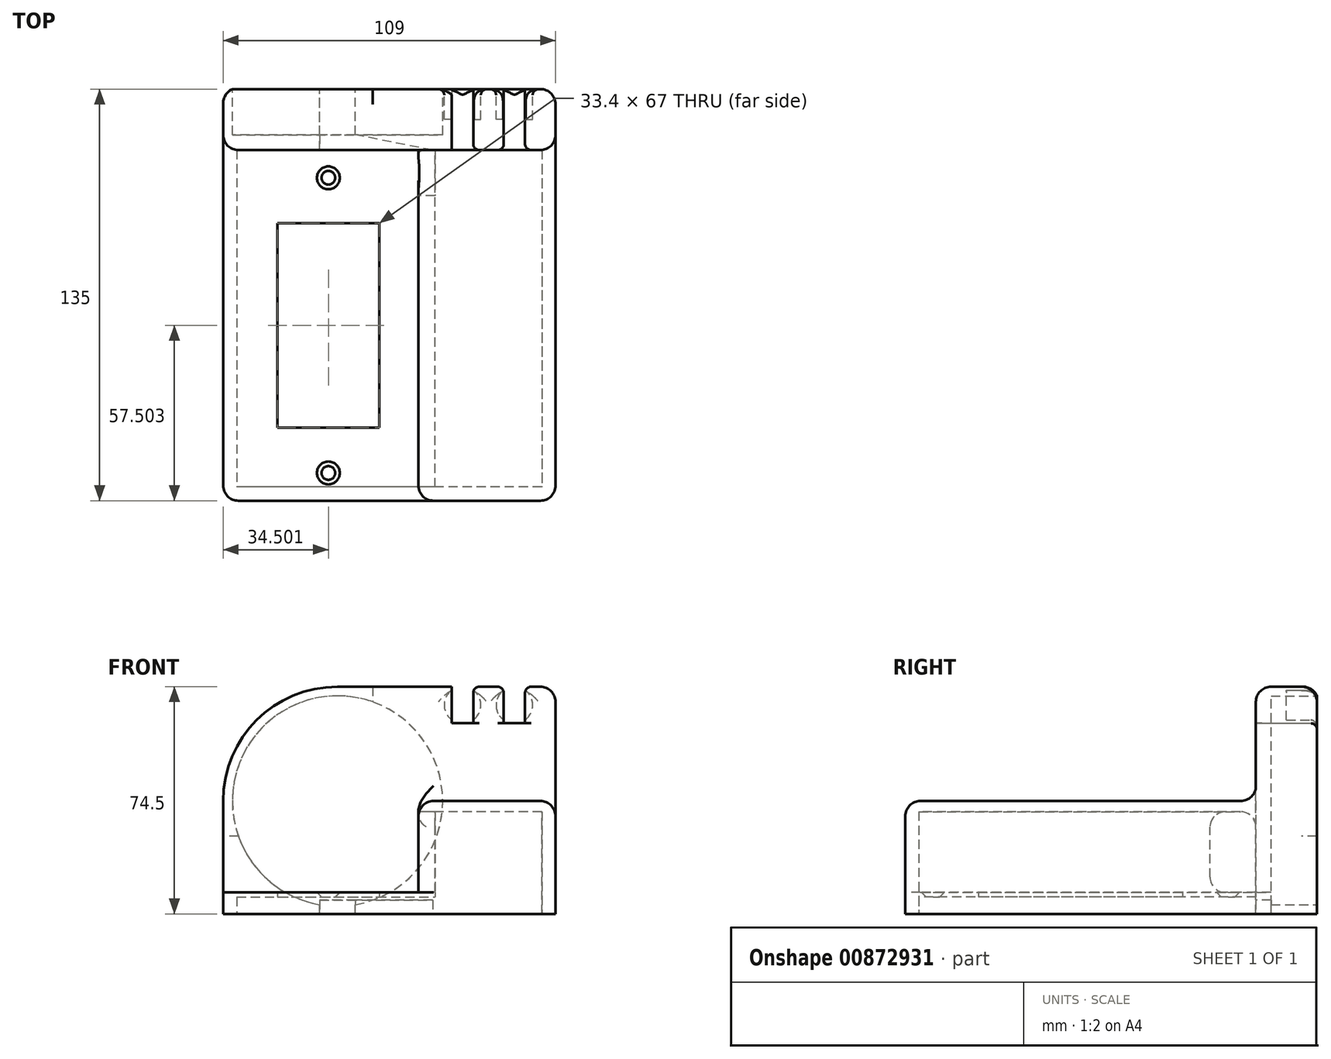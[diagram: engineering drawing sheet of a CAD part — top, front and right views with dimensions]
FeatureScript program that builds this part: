
annotation { "Feature Type Name" : "Feature", "Feature Type Description" : "" }
export const myFeature = defineFeature(function(context is Context, id is Id, definition is map)
    precondition{}
    {
        {
            var Q0;
            Q0=qCreatedBy(makeId("Top.planeOp"),FACE);
            var sketch = newSketch(context, id + "F0", { "sketchPlane" : qUnion([Q0])});
            skLineSegment(sketch, "E0.top", {"start": v(-268.4, -118.47) * mm, "end": v(-199.4, -118.47) * mm});
            skLineSegment(sketch, "E0.left", {"start": v(-268.4, -3.47) * mm, "end": v(-268.4, -118.47) * mm});
            skLineSegment(sketch, "E1.bottom", {"start": v(-217.2, -94.47) * mm, "end": v(-250.6, -94.47) * mm});
            skLineSegment(sketch, "E1.top", {"start": v(-217.2, -27.47) * mm, "end": v(-250.6, -27.47) * mm});
            skLineSegment(sketch, "E1.left", {"start": v(-217.2, -94.47) * mm, "end": v(-217.2, -27.47) * mm});
            skLineSegment(sketch, "E1.right", {"start": v(-250.6, -94.47) * mm, "end": v(-250.6, -27.47) * mm});
            skPoint(sketch, "E1.middle", {"position": v(-233.9, -60.97) * mm});
            skCircle(sketch, "E2", {"center": v(-233.9, -12.57) * mm, "radius": 1.75 * mm});
            skCircle(sketch, "E3", {"center": v(-233.9, -109.37) * mm, "radius": 1.75 * mm});
            skPoint(sketch, "E4.orphan", {"position": v(-233.9, -3.47) * mm});
            skPoint(sketch, "E5.orphan", {"position": v(-233.9, -118.47) * mm});
            skLineSegment(sketch, "E6", {"start": v(-233.9, -12.57) * mm, "end": v(-233.9, -60.97) * mm, "construction": true});
            skLineSegment(sketch, "E7", {"start": v(-233.9, -109.37) * mm, "end": v(-233.9, -60.97) * mm, "construction": true});
            skLineSegment(sketch, "E8.top", {"start": v(-199.4, -118.47) * mm, "end": v(-159.4, -118.47) * mm});
            skLineSegment(sketch, "E8.right", {"start": v(-159.4, -3.47) * mm, "end": v(-159.4, -118.47) * mm});
            skLineSegment(sketch, "E9.top", {"start": v(-268.4, 6.53) * mm, "end": v(-159.4, 6.53) * mm});
            skLineSegment(sketch, "E9.left", {"start": v(-268.4, -3.47) * mm, "end": v(-268.4, 6.53) * mm});
            skLineSegment(sketch, "E9.right", {"start": v(-159.4, -3.47) * mm, "end": v(-159.4, 6.53) * mm});
            skPoint(sketch, "E10.orphan", {"position": v(-199.4, -3.47) * mm});
            skSolve(sketch);
        }
        {
            var Q0;
            Q0 = qSketchRegion(id + "F0", true);
            extrude(context, id + "F1", {"entities" : qUnion([Q0]), "depth" : 4 * mm, "offsetDistance" : 25 * mm});
        }
        {
            var Q0;
            Q0=makeQuery(id+"F1.opExtrude","CAP_FACE",FACE,{"disambiguationData":[OSD([sQuery(id+"F0.wireOp",EDGE,"E0.top"),sQuery(id+"F0.wireOp",EDGE,"E0.left"),sQuery(id+"F0.wireOp",EDGE,"E1.bottom"),sQuery(id+"F0.wireOp",EDGE,"E1.top"),sQuery(id+"F0.wireOp",EDGE,"E1.left"),sQuery(id+"F0.wireOp",EDGE,"E1.right"),sQuery(id+"F0.wireOp",EDGE,"E2"),sQuery(id+"F0.wireOp",EDGE,"E3"),sQuery(id+"F0.wireOp",EDGE,"E8.top"),sQuery(id+"F0.wireOp",EDGE,"E8.right"),sQuery(id+"F0.wireOp",EDGE,"E9.top"),sQuery(id+"F0.wireOp",EDGE,"E9.left"),sQuery(id+"F0.wireOp",EDGE,"E9.right")])],"isStart":true});
            var sketch = newSketch(context, id + "F2", { "sketchPlane" : qUnion([Q0])});
            skLineSegment(sketch, "E11.bottom", {"start": v(-163.9, -2.03) * mm, "end": v(-263.9, -2.03) * mm});
            skLineSegment(sketch, "E11.top", {"start": v(-163.9, 113.97) * mm, "end": v(-263.9, 113.97) * mm});
            skLineSegment(sketch, "E11.left", {"start": v(-163.9, -2.03) * mm, "end": v(-163.9, 113.97) * mm});
            skLineSegment(sketch, "E11.right", {"start": v(-263.9, -2.03) * mm, "end": v(-263.9, 113.97) * mm});
            skPoint(sketch, "E11.middle", {"position": v(-213.9, 55.97) * mm});
            skPoint(sketch, "E11.middle.positionSnap0", {"position": v(-159.4, 55.97) * mm});
            skPoint(sketch, "E11.middle.positionSnap1", {"position": v(-213.9, 118.47) * mm});
            skPoint(sketch, "E11.centerSnap0", {"position": v(-159.4, 55.97) * mm});
            skPoint(sketch, "E11.centerSnap1", {"position": v(-213.9, 118.47) * mm});
            skSolve(sketch);
        }
        {
            var Q0;
            Q0 = qSketchRegion(id + "F2", true);
            extrude(context, id + "F3", {"entities" : qUnion([Q0]), "operationType" : NewBodyOperationType.REMOVE, "oppositeDirection" : true, "depth" : 2.5 * mm, "offsetDistance" : 25 * mm});
        }
        {
            var Q0;
            Q0=makeQuery(id+"F1.opExtrude","CAP_FACE",FACE,{"disambiguationData":[OSD([sQuery(id+"F0.wireOp",EDGE,"E0.top"),sQuery(id+"F0.wireOp",EDGE,"E0.left"),sQuery(id+"F0.wireOp",EDGE,"E1.bottom"),sQuery(id+"F0.wireOp",EDGE,"E1.top"),sQuery(id+"F0.wireOp",EDGE,"E1.left"),sQuery(id+"F0.wireOp",EDGE,"E1.right"),sQuery(id+"F0.wireOp",EDGE,"E2"),sQuery(id+"F0.wireOp",EDGE,"E3"),sQuery(id+"F0.wireOp",EDGE,"E8.top"),sQuery(id+"F0.wireOp",EDGE,"E8.right"),sQuery(id+"F0.wireOp",EDGE,"E9.top"),sQuery(id+"F0.wireOp",EDGE,"E9.left"),sQuery(id+"F0.wireOp",EDGE,"E9.right")])],"isStart":false});
            var sketch = newSketch(context, id + "F4", { "sketchPlane" : qUnion([Q0])});
            skLineSegment(sketch, "E12.bottom", {"start": v(-268.4, 6.53) * mm, "end": v(-159.4, 6.53) * mm});
            skLineSegment(sketch, "E12.top", {"start": v(-268.4, -3.47) * mm, "end": v(-204.4, -3.47) * mm});
            skLineSegment(sketch, "E12.left", {"start": v(-268.4, 6.53) * mm, "end": v(-268.4, -3.47) * mm});
            skLineSegment(sketch, "E12.right", {"start": v(-159.4, 6.53) * mm, "end": v(-159.4, -3.47) * mm});
            skLineSegment(sketch, "E13.top", {"start": v(-159.4, -118.47) * mm, "end": v(-204.4, -118.47) * mm});
            skLineSegment(sketch, "E13.left", {"start": v(-159.4, -3.47) * mm, "end": v(-159.4, -118.47) * mm});
            skLineSegment(sketch, "E13.right", {"start": v(-204.4, -3.47) * mm, "end": v(-204.4, -118.47) * mm});
            skSolve(sketch);
        }
        {
            var Q0;
            Q0 = qSketchRegion(id + "F4", true);
            extrude(context, id + "F5", {"entities" : qUnion([Q0]), "operationType" : NewBodyOperationType.ADD, "depth" : 30 * mm, "offsetDistance" : 25 * mm});
        }
        {
            var Q0;
            Q0=makeQuery(id+"F3.boolean.opBoolean","COPY",FACE,{"derivedFrom":makeQuery(id+"F3.opExtrude","CAP_FACE",FACE,{"disambiguationData":[OSD([sQuery(id+"F2.wireOp",EDGE,"E11.bottom"),sQuery(id+"F2.wireOp",EDGE,"E11.top"),sQuery(id+"F2.wireOp",EDGE,"E11.left"),sQuery(id+"F2.wireOp",EDGE,"E11.right")])],"isStart":false})});
            var sketch = newSketch(context, id + "F6", { "sketchPlane" : qUnion([Q0])});
            skLineSegment(sketch, "E14.bottom", {"start": v(-163.9, 113.97) * mm, "end": v(-198.9, 113.97) * mm});
            skLineSegment(sketch, "E14.top", {"start": v(-163.9, -2.03) * mm, "end": v(-198.9, -2.03) * mm});
            skLineSegment(sketch, "E14.left", {"start": v(-163.9, 113.97) * mm, "end": v(-163.9, -2.03) * mm});
            skLineSegment(sketch, "E14.right", {"start": v(-198.9, 113.97) * mm, "end": v(-198.9, -2.03) * mm});
            skSolve(sketch);
        }
        {
            var Q0;
            Q0=makeQuery(id+"F6.imprint","IMPRINT",FACE,{"disambiguationData":[TD([[makeQuery(id+"F6.imprint","IMPRINT",EDGE,{"derivedFrom":sQuery(id+"F6.wireOp",EDGE,"E14.bottom")}),1.0]])]});
            extrude(context, id + "F7", {"entities" : qUnion([Q0]), "operationType" : NewBodyOperationType.REMOVE, "oppositeDirection" : true, "depth" : 28 * mm, "offsetDistance" : 25 * mm});
        }
        {
            var Q0;
            Q0=makeQuery(id+"F5.opExtrude","SWEPT_FACE",FACE,{"disambiguationData":[OSD([sQuery(id+"F4.wireOp",EDGE,"E13.right")])]});
            var sketch = newSketch(context, id + "F8", { "sketchPlane" : qUnion([Q0])});
            skLineSegment(sketch, "E15.bottom", {"start": v(3.47, 4) * mm, "end": v(18.47, 4) * mm});
            skLineSegment(sketch, "E15.top", {"start": v(3.47, 30.5) * mm, "end": v(18.47, 30.5) * mm});
            skLineSegment(sketch, "E15.left", {"start": v(3.47, 4) * mm, "end": v(3.47, 30.5) * mm});
            skLineSegment(sketch, "E15.right", {"start": v(18.47, 4) * mm, "end": v(18.47, 30.5) * mm});
            skSolve(sketch);
        }
        {
            var Q0;
            Q0 = qSketchRegion(id + "F8", true);
            extrude(context, id + "F9", {"entities" : qUnion([Q0]), "operationType" : NewBodyOperationType.REMOVE, "oppositeDirection" : true, "depth" : 25 * mm, "offsetDistance" : 25 * mm});
        }
        {
            var Q0;
            Q0=makeQuery(id+"F5.boolean.opBoolean","MERGE",FACE,{"derivedFrom":[makeQuery(id+"F1.opExtrude","SWEPT_FACE",FACE,{"disambiguationData":[OSD([sQuery(id+"F0.wireOp",EDGE,"E9.top")])]}),makeQuery(id+"F5.opExtrude","SWEPT_FACE",FACE,{"disambiguationData":[OSD([sQuery(id+"F4.wireOp",EDGE,"E12.bottom")])]})]});
            var sketch = newSketch(context, id + "F10", { "sketchPlane" : qUnion([Q0])});
            skCircle(sketch, "E16", {"center": v(230.9, 34) * mm, "radius": 34.5 * mm, "construction": true});
            skArc(sketch, "E17", {"start": v(268.4, 34) * mm, "mid": v(257.43, 60.52) * mm, "end": v(230.9, 71.5) * mm});
            skLineSegment(sketch, "E18.top", {"start": v(159.4, 0) * mm, "end": v(268.4, 0) * mm});
            skLineSegment(sketch, "E18.left", {"start": v(159.4, 34) * mm, "end": v(159.4, 0) * mm});
            skLineSegment(sketch, "E18.right", {"start": v(268.4, 46) * mm, "end": v(268.4, 0) * mm});
            skLineSegment(sketch, "E19.top", {"start": v(159.4, 71.5) * mm, "end": v(230.9, 71.5) * mm});
            skLineSegment(sketch, "E19.left", {"start": v(159.4, 34) * mm, "end": v(159.4, 71.5) * mm});
            skSolve(sketch);
        }
        {
            var Q0;
            Q0 = qSketchRegion(id + "F10", true);
            extrude(context, id + "F11", {"entities" : qUnion([Q0]), "operationType" : NewBodyOperationType.ADD, "oppositeDirection" : true, "depth" : 10 * mm, "offsetDistance" : 25 * mm, "hasSecondDirection" : true, "secondDirectionOppositeDirection" : false, "secondDirectionDepth" : 10 * mm});
        }
        {
            var Q0;
            Q0=makeQuery(id+"F11.opExtrude","CAP_FACE",FACE,{"disambiguationData":[OSD([sQuery(id+"F10.wireOp",EDGE,"E17"),sQuery(id+"F10.wireOp",EDGE,"E18.bottom"),sQuery(id+"F10.wireOp",EDGE,"E18.top"),sQuery(id+"F10.wireOp",EDGE,"E18.left"),sQuery(id+"F10.wireOp",EDGE,"E18.right")])],"isStart":true});
            var sketch = newSketch(context, id + "F12", { "sketchPlane" : qUnion([Q0])});
            skArc(sketch, "E20", {"start": v(234.9, -0.27) * mm, "mid": v(230.9, 68.5) * mm, "end": v(226.9, -0.27) * mm});
            skLineSegment(sketch, "E21.bottom", {"start": v(234.9, -15.63) * mm, "end": v(226.9, -15.63) * mm});
            skLineSegment(sketch, "E21.left", {"start": v(234.9, -15.63) * mm, "end": v(234.9, -0.27) * mm});
            skLineSegment(sketch, "E21.right", {"start": v(226.9, -15.63) * mm, "end": v(226.9, -0.27) * mm});
            skPoint(sketch, "E22.orphan", {"position": v(226.9, 83.63) * mm});
            skPoint(sketch, "E23.orphan", {"position": v(234.9, 83.63) * mm});
            skSolve(sketch);
        }
        {
            var Q0;
            Q0 = qSketchRegion(id + "F12", true);
            extrude(context, id + "F13", {"entities" : qUnion([Q0]), "operationType" : NewBodyOperationType.REMOVE, "oppositeDirection" : true, "depth" : 15 * mm, "offsetDistance" : 25 * mm});
        }
        {
            var Q0;
            Q0=makeQuery(id+"F11.opExtrude","SWEPT_FACE",FACE,{"disambiguationData":[OSD([sQuery(id+"F10.wireOp",EDGE,"E19.top")])]});
            var sketch = newSketch(context, id + "F14", { "sketchPlane" : qUnion([Q0])});
            skLineSegment(sketch, "E24.bottom", {"start": v(-169.4, -3.47) * mm, "end": v(-176.4, -3.47) * mm});
            skLineSegment(sketch, "E24.top", {"start": v(-169.4, 16.53) * mm, "end": v(-176.4, 16.53) * mm});
            skLineSegment(sketch, "E24.left", {"start": v(-169.4, -3.47) * mm, "end": v(-169.4, 16.53) * mm});
            skLineSegment(sketch, "E24.right", {"start": v(-176.4, -3.47) * mm, "end": v(-176.4, 16.53) * mm});
            skLineSegment(sketch, "E25", {"start": v(-159.4, 6.53) * mm, "end": v(-169.4, 6.53) * mm, "construction": true});
            skLineSegment(sketch, "E26", {"start": v(-176.4, 6.53) * mm, "end": v(-186.4, 6.53) * mm, "construction": true});
            skPoint(sketch, "E26.endSnap0", {"position": v(-176.4, 6.53) * mm});
            skLineSegment(sketch, "E27.bottom", {"start": v(-186.4, -3.47) * mm, "end": v(-193.4, -3.47) * mm});
            skLineSegment(sketch, "E27.top", {"start": v(-186.4, 16.53) * mm, "end": v(-193.4, 16.53) * mm});
            skLineSegment(sketch, "E27.left", {"start": v(-186.4, -3.47) * mm, "end": v(-186.4, 16.53) * mm});
            skLineSegment(sketch, "E27.right", {"start": v(-193.4, -3.47) * mm, "end": v(-193.4, 16.53) * mm});
            skSolve(sketch);
        }
        {
            var Q0;
            Q0 = qSketchRegion(id + "F14", true);
            extrude(context, id + "F15", {"entities" : qUnion([Q0]), "operationType" : NewBodyOperationType.REMOVE, "oppositeDirection" : true, "depth" : 12 * mm, "offsetDistance" : 25 * mm});
        }
        {
            var Q0;
            Q0=makeQuery(id+"F1Z2qfNy66yVWWs_1.boolean.opBoolean","MERGE",FACE,{"derivedFrom":[makeQuery(id+"F11.opExtrude","CAP_FACE",FACE,{"disambiguationData":[OSD([sQuery(id+"F10.wireOp",EDGE,"E17"),sQuery(id+"F10.wireOp",EDGE,"E18.top"),sQuery(id+"F10.wireOp",EDGE,"E18.left"),sQuery(id+"F10.wireOp",EDGE,"E18.right"),sQuery(id+"F10.wireOp",EDGE,"E19.top"),sQuery(id+"F10.wireOp",EDGE,"E19.left")])],"isStart":true}),makeQuery(id+"F1Z2qfNy66yVWWs_1.opExtrude","SWEPT_FACE",FACE,{"disambiguationData":[OSD([sQuery(id+"FdsJ3Gxod82OhhE_1.wireOp",EDGE,"4jFBjwjJ-6N3J-Dahm-4fYq-youUggST2oqY.top")])]}),makeQuery(id+"F1Z2qfNy66yVWWs_1.opExtrude","SWEPT_FACE",FACE,{"disambiguationData":[OSD([sQuery(id+"FdsJ3Gxod82OhhE_1.wireOp",EDGE,"be54c355-b7a8-450f-9b8c-2efa35130c0c.trimOffspring")])]})]});
            var sketch = newSketch(context, id + "F16", { "sketchPlane" : qUnion([Q0])});
            skCircle(sketch, "E28", {"center": v(172.9, 65.5) * mm, "radius": 6 * mm});
            skPoint(sketch, "E28.centerSnap0", {"position": v(172.9, 59.5) * mm});
            skPoint(sketch, "E28.centerSnap1", {"position": v(169.4, 65.5) * mm});
            skCircle(sketch, "E29", {"center": v(189.9, 65.5) * mm, "radius": 6 * mm});
            skPoint(sketch, "E29.centerSnap0", {"position": v(186.4, 65.5) * mm});
            skPoint(sketch, "E29.centerSnap1", {"position": v(189.9, 59.5) * mm});
            skSolve(sketch);
        }
        {
            var Q0;
            Q0 = qSketchRegion(id + "F16", true);
            extrude(context, id + "F17", {"entities" : qUnion([Q0]), "operationType" : NewBodyOperationType.REMOVE, "oppositeDirection" : true, "depth" : 10 * mm, "offsetDistance" : 25 * mm});
        }
        {
            var Q0;
            Q0=makeQuery(id+"F11.boolean.opBoolean","MERGE",FACE,{"derivedFrom":[makeQuery(id+"F1.opExtrude","CAP_FACE",FACE,{"disambiguationData":[OSD([sQuery(id+"F0.wireOp",EDGE,"E0.top"),sQuery(id+"F0.wireOp",EDGE,"E0.left"),sQuery(id+"F0.wireOp",EDGE,"E1.bottom"),sQuery(id+"F0.wireOp",EDGE,"E1.top"),sQuery(id+"F0.wireOp",EDGE,"E1.left"),sQuery(id+"F0.wireOp",EDGE,"E1.right"),sQuery(id+"F0.wireOp",EDGE,"E2"),sQuery(id+"F0.wireOp",EDGE,"E3"),sQuery(id+"F0.wireOp",EDGE,"E8.top"),sQuery(id+"F0.wireOp",EDGE,"E8.right"),sQuery(id+"F0.wireOp",EDGE,"E9.top"),sQuery(id+"F0.wireOp",EDGE,"E9.left"),sQuery(id+"F0.wireOp",EDGE,"E9.right")])],"isStart":true}),makeQuery(id+"F11.opExtrude","SWEPT_FACE",FACE,{"disambiguationData":[OSD([sQuery(id+"F10.wireOp",EDGE,"E18.top")])]})]});
            var sketch = newSketch(context, id + "F18", { "sketchPlane" : qUnion([Q0])});
            skLineSegment(sketch, "E30", {"start": v(-236.76, -1.53) * mm, "end": v(-236.76, 3.47) * mm});
            skLineSegment(sketch, "E31", {"start": v(-236.76, 3.47) * mm, "end": v(-199.75, 3.47) * mm});
            skLineSegment(sketch, "E32", {"start": v(-199.75, 3.47) * mm, "end": v(-225.06, -1.53) * mm});
            skLineSegment(sketch, "E33", {"start": v(-225.06, -1.53) * mm, "end": v(-236.76, -1.53) * mm});
            skSolve(sketch);
        }
        {
            var Q0;
            Q0 = qSketchRegion(id + "F18", true);
            extrude(context, id + "F19", {"entities" : qUnion([Q0]), "operationType" : NewBodyOperationType.REMOVE, "oppositeDirection" : true, "depth" : 1.5 * mm, "offsetDistance" : 25 * mm});
        }
        {
            var Q0;
            Q0=makeQuery(id+"F11.boolean.opBoolean","MERGE",FACE,{"derivedFrom":[makeQuery(id+"F1.opExtrude","CAP_FACE",FACE,{"disambiguationData":[OSD([sQuery(id+"F0.wireOp",EDGE,"E0.top"),sQuery(id+"F0.wireOp",EDGE,"E0.left"),sQuery(id+"F0.wireOp",EDGE,"E1.bottom"),sQuery(id+"F0.wireOp",EDGE,"E1.top"),sQuery(id+"F0.wireOp",EDGE,"E1.left"),sQuery(id+"F0.wireOp",EDGE,"E1.right"),sQuery(id+"F0.wireOp",EDGE,"E2"),sQuery(id+"F0.wireOp",EDGE,"E3"),sQuery(id+"F0.wireOp",EDGE,"E8.top"),sQuery(id+"F0.wireOp",EDGE,"E8.right"),sQuery(id+"F0.wireOp",EDGE,"E9.top"),sQuery(id+"F0.wireOp",EDGE,"E9.left"),sQuery(id+"F0.wireOp",EDGE,"E9.right")])],"isStart":true}),makeQuery(id+"F11.opExtrude","SWEPT_FACE",FACE,{"disambiguationData":[OSD([sQuery(id+"F10.wireOp",EDGE,"E18.top")])]})]});
            var sketch = newSketch(context, id + "F20", { "sketchPlane" : qUnion([Q0])});
            skLineSegment(sketch, "E34.bottom", {"start": v(-159.4, 118.47) * mm, "end": v(-268.4, 118.47) * mm});
            skLineSegment(sketch, "E34.top", {"start": v(-159.4, -16.53) * mm, "end": v(-225.06, -16.53) * mm});
            skLineSegment(sketch, "E34.left", {"start": v(-159.4, 118.47) * mm, "end": v(-159.4, -16.53) * mm});
            skLineSegment(sketch, "E34.right", {"start": v(-268.4, 118.47) * mm, "end": v(-268.4, -16.53) * mm});
            skLineSegment(sketch, "E35.bottom", {"start": v(-263.9, 113.97) * mm, "end": v(-163.9, 113.97) * mm});
            skLineSegment(sketch, "E35.top", {"start": v(-263.9, 3.47) * mm, "end": v(-236.76, 3.47) * mm});
            skLineSegment(sketch, "E35.left", {"start": v(-263.9, 113.97) * mm, "end": v(-263.9, 3.47) * mm});
            skLineSegment(sketch, "E35.right", {"start": v(-163.9, 113.97) * mm, "end": v(-163.9, 3.47) * mm});
            skLineSegment(sketch, "E36", {"start": v(-236.76, 3.47) * mm, "end": v(-236.76, -16.53) * mm});
            skLineSegment(sketch, "E37", {"start": v(-225.06, -16.53) * mm, "end": v(-225.06, -1.53) * mm});
            skLineSegment(sketch, "E38", {"start": v(-225.06, -1.53) * mm, "end": v(-199.75, 3.47) * mm});
            skLineSegment(sketch, "E39.trimOffspring", {"start": v(-199.75, 3.47) * mm, "end": v(-163.9, 3.47) * mm});
            skLineSegment(sketch, "E40.trimOffspring", {"start": v(-236.76, -16.53) * mm, "end": v(-268.4, -16.53) * mm});
            skSolve(sketch);
        }
        {
            var Q0;
            Q0 = qSketchRegion(id + "F20", true);
            extrude(context, id + "F21", {"entities" : qUnion([Q0]), "operationType" : NewBodyOperationType.ADD, "depth" : 3 * mm, "offsetDistance" : 25 * mm});
        }
        {
            var Q0;
            Q0=makeQuery(id+"F21.boolean.opBoolean","MERGE",EDGE,{"derivedFrom":[makeQuery(id+"F1.opExtrude","SWEPT_EDGE",EDGE,{"disambiguationData":[OSD([sQuery(id+"F0.wireOp",EDGE,"E0.top"),sQuery(id+"F0.wireOp",EDGE,"E0.left")])]}),makeQuery(id+"F21.opExtrude","SWEPT_EDGE",EDGE,{"disambiguationData":[OSD([sQuery(id+"F20.wireOp",EDGE,"E34.bottom"),sQuery(id+"F20.wireOp",EDGE,"E34.right")])]})]});
            var Q1;
            Q1=makeQuery(id+"F21.boolean.opBoolean","MERGE",EDGE,{"derivedFrom":[makeQuery(id+"F5.boolean.opBoolean","MERGE",EDGE,{"derivedFrom":[makeQuery(id+"F1.opExtrude","SWEPT_EDGE",EDGE,{"disambiguationData":[OSD([sQuery(id+"F0.wireOp",EDGE,"E8.top"),sQuery(id+"F0.wireOp",EDGE,"E8.right")])]}),makeQuery(id+"F5.opExtrude","SWEPT_EDGE",EDGE,{"disambiguationData":[OSD([sQuery(id+"F4.wireOp",EDGE,"E13.top"),sQuery(id+"F4.wireOp",EDGE,"E13.left")])]})]}),makeQuery(id+"F21.opExtrude","SWEPT_EDGE",EDGE,{"disambiguationData":[OSD([sQuery(id+"F20.wireOp",EDGE,"E34.bottom"),sQuery(id+"F20.wireOp",EDGE,"E34.left")])]})]});
            var Q2;
            Q2=makeQuery(id+"F5.opExtrude","SWEPT_EDGE",EDGE,{"disambiguationData":[OSD([sQuery(id+"F0.wireOp",EDGE,"E0.top"),sQuery(id+"F0.wireOp",EDGE,"E8.top"),sQuery(id+"F4.wireOp",EDGE,"E13.top"),sQuery(id+"F4.wireOp",EDGE,"E13.right")])]});
            var Q3;
            Q3=makeQuery(id+"F21.boolean.opBoolean","MERGE",EDGE,{"derivedFrom":[makeQuery(id+"F11.opExtrude","CAP_EDGE",EDGE,{"disambiguationData":[OSD([sQuery(id+"F10.wireOp",EDGE,"E18.right")])],"isStart":true}),makeQuery(id+"F21.opExtrude","SWEPT_EDGE",EDGE,{"disambiguationData":[OSD([sQuery(id+"F20.wireOp",EDGE,"E34.right"),sQuery(id+"F20.wireOp",EDGE,"E40.trimOffspring")])]})]});
            var Q4;
            Q4=makeQuery(id+"F11.opExtrude","SWEPT_EDGE",EDGE,{"disambiguationData":[OSD([sQuery(id+"F10.wireOp",EDGE,"E19.top"),sQuery(id+"F10.wireOp",EDGE,"E19.left")])]});
            var Q5;
            Q5=makeQuery(id+"F21.boolean.opBoolean","MERGE",EDGE,{"derivedFrom":[makeQuery(id+"F11.opExtrude","CAP_EDGE",EDGE,{"disambiguationData":[OSD([sQuery(id+"F10.wireOp",EDGE,"E18.left"),sQuery(id+"F10.wireOp",EDGE,"E19.left")])],"isStart":true}),makeQuery(id+"F21.opExtrude","SWEPT_EDGE",EDGE,{"disambiguationData":[OSD([sQuery(id+"F20.wireOp",EDGE,"E34.top"),sQuery(id+"F20.wireOp",EDGE,"E34.left")])]})]});
            var Q6;
            Q6=makeQuery(id+"F11.opExtrude","CAP_EDGE",EDGE,{"disambiguationData":[OSD([sQuery(id+"F10.wireOp",EDGE,"E18.left"),sQuery(id+"F10.wireOp",EDGE,"E19.left")])],"isStart":false});
            var Q7;
            Q7=makeQuery(id+"F5.opExtrude","CAP_EDGE",EDGE,{"disambiguationData":[OSD([sQuery(id+"F4.wireOp",EDGE,"E12.right"),sQuery(id+"F4.wireOp",EDGE,"E13.left")])],"isStart":false});
            var Q8;
            Q8=makeQuery(id+"F11.boolean.opBoolean","INTERSECT",EDGE,{"derivedFrom":[makeQuery(id+"F5.opExtrude","CAP_FACE",FACE,{"disambiguationData":[OSD([sQuery(id+"F4.wireOp",EDGE,"E12.bottom"),sQuery(id+"F4.wireOp",EDGE,"E12.top"),sQuery(id+"F4.wireOp",EDGE,"E12.left"),sQuery(id+"F4.wireOp",EDGE,"E12.right"),sQuery(id+"F4.wireOp",EDGE,"E13.top"),sQuery(id+"F4.wireOp",EDGE,"E13.left"),sQuery(id+"F4.wireOp",EDGE,"E13.right")])],"isStart":false}),makeQuery(id+"F11.opExtrude","CAP_FACE",FACE,{"disambiguationData":[OSD([sQuery(id+"F10.wireOp",EDGE,"E17"),sQuery(id+"F10.wireOp",EDGE,"E18.top"),sQuery(id+"F10.wireOp",EDGE,"E18.left"),sQuery(id+"F10.wireOp",EDGE,"E18.right"),sQuery(id+"F10.wireOp",EDGE,"E19.top"),sQuery(id+"F10.wireOp",EDGE,"E19.left")])],"isStart":false})]});
            var Q9;
            Q9=makeQuery(id+"F5.opExtrude","CAP_EDGE",EDGE,{"disambiguationData":[OSD([sQuery(id+"F4.wireOp",EDGE,"E13.right")])],"isStart":true});
            var Q10;
            Q10=makeQuery(id+"F5.opExtrude","CAP_EDGE",EDGE,{"disambiguationData":[OSD([sQuery(id+"F4.wireOp",EDGE,"E13.top")])],"isStart":false});
            var Q11;
            Q11=makeQuery(id+"F9.boolean.opBoolean","MERGE",EDGE,{"derivedFrom":[makeQuery(id+"F5.opExtrude","CAP_EDGE",EDGE,{"disambiguationData":[OSD([sQuery(id+"F4.wireOp",EDGE,"E12.top")])],"isStart":true}),makeQuery(id+"F9.opExtrude","SWEPT_EDGE",EDGE,{"disambiguationData":[OSD([sQuery(id+"F8.wireOp",EDGE,"E15.bottom"),sQuery(id+"F8.wireOp",EDGE,"E15.left")])]})]});
            var Q12;
            Q12=makeQuery(id+"F11.opExtrude","CAP_EDGE",EDGE,{"disambiguationData":[OSD([sQuery(id+"F10.wireOp",EDGE,"E17")])],"isStart":false});
            var Q13;
            {var subQ0=sQuery(id+"F10.wireOp",EDGE,"E19.top");Q13=makeQuery(id+"F15.boolean.opBoolean","SPLIT",EDGE,{"disambiguationData":[TD([makeQuery(id+"F15.opExtrude","SWEPT_FACE",FACE,{"disambiguationData":[OSD([sQuery(id+"F14.wireOp",EDGE,"E24.right")])]})])],"derivedFrom":makeQuery(id+"F11.opExtrude","CAP_EDGE",EDGE,{"disambiguationData":[OSD([subQ0])],"isStart":false})});}
            var Q14;
            {var subQ1=sQuery(id+"F10.wireOp",EDGE,"E19.top");Q14=makeQuery(id+"F15.boolean.opBoolean","SPLIT",EDGE,{"disambiguationData":[TD([makeQuery(id+"F15.opExtrude","SWEPT_FACE",FACE,{"disambiguationData":[OSD([sQuery(id+"F14.wireOp",EDGE,"E24.left")])]})])],"derivedFrom":makeQuery(id+"F11.opExtrude","CAP_EDGE",EDGE,{"disambiguationData":[OSD([subQ1])],"isStart":false})});}
            var Q15;
            {var subQ0=sQuery(id+"F10.wireOp",EDGE,"E19.top");Q15=makeQuery(id+"F15.boolean.opBoolean","SPLIT",EDGE,{"disambiguationData":[TD([makeQuery(id+"F15.opExtrude","SWEPT_FACE",FACE,{"disambiguationData":[OSD([sQuery(id+"F14.wireOp",EDGE,"E24.right")])]})])],"derivedFrom":makeQuery(id+"F11.opExtrude","CAP_EDGE",EDGE,{"disambiguationData":[OSD([subQ0])],"isStart":true})});}
            var Q16;
            {var subQ2=sQuery(id+"F10.wireOp",EDGE,"E19.top");Q16=makeQuery(id+"F15.boolean.opBoolean","SPLIT",EDGE,{"disambiguationData":[TD([makeQuery(id+"F15.opExtrude","SWEPT_FACE",FACE,{"disambiguationData":[OSD([sQuery(id+"F14.wireOp",EDGE,"E24.left")])]})])],"derivedFrom":makeQuery(id+"F11.opExtrude","CAP_EDGE",EDGE,{"disambiguationData":[OSD([subQ2])],"isStart":true})});}
            var Q17;
            Q17=makeQuery(id+"F13.boolean.opBoolean","COPY",EDGE,{"derivedFrom":makeQuery(id+"F13.opExtrude","CAP_EDGE",EDGE,{"disambiguationData":[OSD([sQuery(id+"F12.wireOp",EDGE,"E20")])],"isStart":true})});
            fillet(context, id + "F22", {"entities" : qUnion([Q0, Q1, Q2, Q3, Q4, Q5, Q6, Q7, Q8, Q9, Q10, Q11, Q12, Q13, Q14, Q15, Q16, Q17]), "radius" : 5 * mm, "tangentPropagation" : true, "allowEdgeOverflow" : false});
        }
        {
            var Q0;
            Q0=makeQuery(id+"F5.opExtrude","CAP_EDGE",EDGE,{"disambiguationData":[OSD([sQuery(id+"F4.wireOp",EDGE,"E13.right")])],"isStart":false});
            fillet(context, id + "F23", {"entities" : qUnion([Q0]), "radius" : 5 * mm, "tangentPropagation" : true, "allowEdgeOverflow" : false});
        }
        {
            var Q0;
            Q0=makeQuery(id+"F9.boolean.opBoolean","COPY",EDGE,{"derivedFrom":makeQuery(id+"F9.opExtrude","SWEPT_EDGE",EDGE,{"disambiguationData":[OSD([sQuery(id+"F4.wireOp",EDGE,"E13.right"),sQuery(id+"F8.wireOp",EDGE,"E15.bottom"),sQuery(id+"F8.wireOp",EDGE,"E15.right")])]})});
            var Q1;
            Q1=makeQuery(id+"F9.boolean.opBoolean","COPY",EDGE,{"derivedFrom":makeQuery(id+"F9.opExtrude","SWEPT_EDGE",EDGE,{"disambiguationData":[OSD([sQuery(id+"F8.wireOp",EDGE,"E15.top"),sQuery(id+"F8.wireOp",EDGE,"E15.right")])]})});
            var Q2;
            Q2=makeQuery(id+"F11.boolean.opBoolean","INTERSECT",EDGE,{"derivedFrom":[makeQuery(id+"F9.boolean.opBoolean","MERGE",FACE,{"derivedFrom":[makeQuery(id+"F7.boolean.opBoolean","COPY",FACE,{"derivedFrom":makeQuery(id+"F7.opExtrude","CAP_FACE",FACE,{"disambiguationData":[OSD([sQuery(id+"F6.wireOp",EDGE,"E14.bottom"),sQuery(id+"F6.wireOp",EDGE,"E14.top"),sQuery(id+"F6.wireOp",EDGE,"E14.left"),sQuery(id+"F6.wireOp",EDGE,"E14.right")])],"isStart":false})}),makeQuery(id+"F9.opExtrude","SWEPT_FACE",FACE,{"disambiguationData":[OSD([sQuery(id+"F8.wireOp",EDGE,"E15.top")])]})]}),makeQuery(id+"F11.opExtrude","CAP_FACE",FACE,{"disambiguationData":[OSD([sQuery(id+"F10.wireOp",EDGE,"E17"),sQuery(id+"F10.wireOp",EDGE,"E18.top"),sQuery(id+"F10.wireOp",EDGE,"E18.left"),sQuery(id+"F10.wireOp",EDGE,"E18.right"),sQuery(id+"F10.wireOp",EDGE,"E19.top"),sQuery(id+"F10.wireOp",EDGE,"E19.left")])],"isStart":false})]});
            fillet(context, id + "F24", {"entities" : qUnion([Q0, Q1, Q2]), "radius" : 5 * mm, "tangentPropagation" : true, "allowEdgeOverflow" : false});
        }
        {
            var Q0;
            {var subQ0=sQuery(id+"F10.wireOp",EDGE,"E19.top");var subQ2=makeQuery(id+"F15.opExtrude","SWEPT_FACE",FACE,{"disambiguationData":[OSD([sQuery(id+"F14.wireOp",EDGE,"E27.left")])]});var subQ3=sQuery(id+"F16.wireOp",EDGE,"E29");Q0=makeQuery(id+"F22.opFillet","BLEND_EDGE",EDGE,{"blendedFrom":[makeQuery(id+"F15.boolean.opBoolean","SPLIT",EDGE,{"disambiguationData":[TD([makeQuery(id+"F15.opExtrude","SWEPT_FACE",FACE,{"disambiguationData":[OSD([sQuery(id+"F14.wireOp",EDGE,"E24.right")])]})])],"derivedFrom":makeQuery(id+"F11.opExtrude","CAP_EDGE",EDGE,{"disambiguationData":[OSD([subQ0])],"isStart":true})}),makeQuery(id+"F17.boolean.opBoolean","COPY",FACE,{"disambiguationData":[TD([makeQuery(id+"F15.boolean.opBoolean","COPY",FACE,{"derivedFrom":subQ2})])],"derivedFrom":makeQuery(id+"F17.opExtrude","SWEPT_FACE",FACE,{"disambiguationData":[OSD([subQ3])]})})],"blendedInto":[makeQuery(id+"F17.boolean.opBoolean","COPY",FACE,{"disambiguationData":[TD([makeQuery(id+"F15.boolean.opBoolean","COPY",FACE,{"derivedFrom":subQ2})])],"derivedFrom":makeQuery(id+"F17.opExtrude","SWEPT_FACE",FACE,{"disambiguationData":[OSD([subQ3])]})})]});}
            var Q1;
            {var subQ1=sQuery(id+"F10.wireOp",EDGE,"E19.top");var subQ4=makeQuery(id+"F15.opExtrude","SWEPT_FACE",FACE,{"disambiguationData":[OSD([sQuery(id+"F14.wireOp",EDGE,"E24.left")])]});var subQ5=sQuery(id+"F16.wireOp",EDGE,"E28");Q1=makeQuery(id+"F22.opFillet","BLEND_EDGE",EDGE,{"blendedFrom":[makeQuery(id+"F15.boolean.opBoolean","SPLIT",EDGE,{"disambiguationData":[TD([subQ4])],"derivedFrom":makeQuery(id+"F11.opExtrude","CAP_EDGE",EDGE,{"disambiguationData":[OSD([subQ1])],"isStart":true})}),makeQuery(id+"F17.boolean.opBoolean","COPY",FACE,{"disambiguationData":[TD([makeQuery(id+"F15.boolean.opBoolean","COPY",FACE,{"derivedFrom":subQ4})])],"derivedFrom":makeQuery(id+"F17.opExtrude","SWEPT_FACE",FACE,{"disambiguationData":[OSD([subQ5])]})})],"blendedInto":[makeQuery(id+"F17.boolean.opBoolean","COPY",FACE,{"disambiguationData":[TD([makeQuery(id+"F15.boolean.opBoolean","COPY",FACE,{"derivedFrom":subQ4})])],"derivedFrom":makeQuery(id+"F17.opExtrude","SWEPT_FACE",FACE,{"disambiguationData":[OSD([subQ5])]})})]});}
            fillet(context, id + "F25", {"entities" : qUnion([Q0, Q1]), "radius" : 2 * mm, "tangentPropagation" : true, "allowEdgeOverflow" : false});
        }
        {
            var Q0;
            Q0=makeQuery(id+"F15.boolean.opBoolean","COPY",EDGE,{"derivedFrom":makeQuery(id+"F15.opExtrude","CAP_EDGE",EDGE,{"disambiguationData":[OSD([sQuery(id+"F14.wireOp",EDGE,"E24.right")])],"isStart":true})});
            var Q1;
            Q1=makeQuery(id+"F15.boolean.opBoolean","COPY",EDGE,{"derivedFrom":makeQuery(id+"F15.opExtrude","CAP_EDGE",EDGE,{"disambiguationData":[OSD([sQuery(id+"F14.wireOp",EDGE,"E27.left")])],"isStart":true})});
            var Q2;
            Q2=makeQuery(id+"F15.boolean.opBoolean","COPY",EDGE,{"derivedFrom":makeQuery(id+"F15.opExtrude","CAP_EDGE",EDGE,{"disambiguationData":[OSD([sQuery(id+"F14.wireOp",EDGE,"E24.left")])],"isStart":true})});
            var Q3;
            Q3=makeQuery(id+"F15.boolean.opBoolean","COPY",EDGE,{"derivedFrom":makeQuery(id+"F15.opExtrude","CAP_EDGE",EDGE,{"disambiguationData":[OSD([sQuery(id+"F14.wireOp",EDGE,"E27.right")])],"isStart":true})});
            fillet(context, id + "F26", {"entities" : qUnion([Q0, Q1, Q2, Q3]), "radius" : 2 * mm, "tangentPropagation" : true, "allowEdgeOverflow" : false});
        }
        {
            var Q0;
            Q0=makeQuery(id+"F1.opExtrude","CAP_EDGE",EDGE,{"disambiguationData":[OSD([sQuery(id+"F0.wireOp",EDGE,"E2")])],"isStart":false});
            var Q1;
            Q1=makeQuery(id+"F1.opExtrude","CAP_EDGE",EDGE,{"disambiguationData":[OSD([sQuery(id+"F0.wireOp",EDGE,"E3")])],"isStart":false});
            chamfer(context, id + "F27", {"entities" : qUnion([Q0, Q1]), "width" : 2 * mm, "tangentPropagation" : true});
        }
    });
